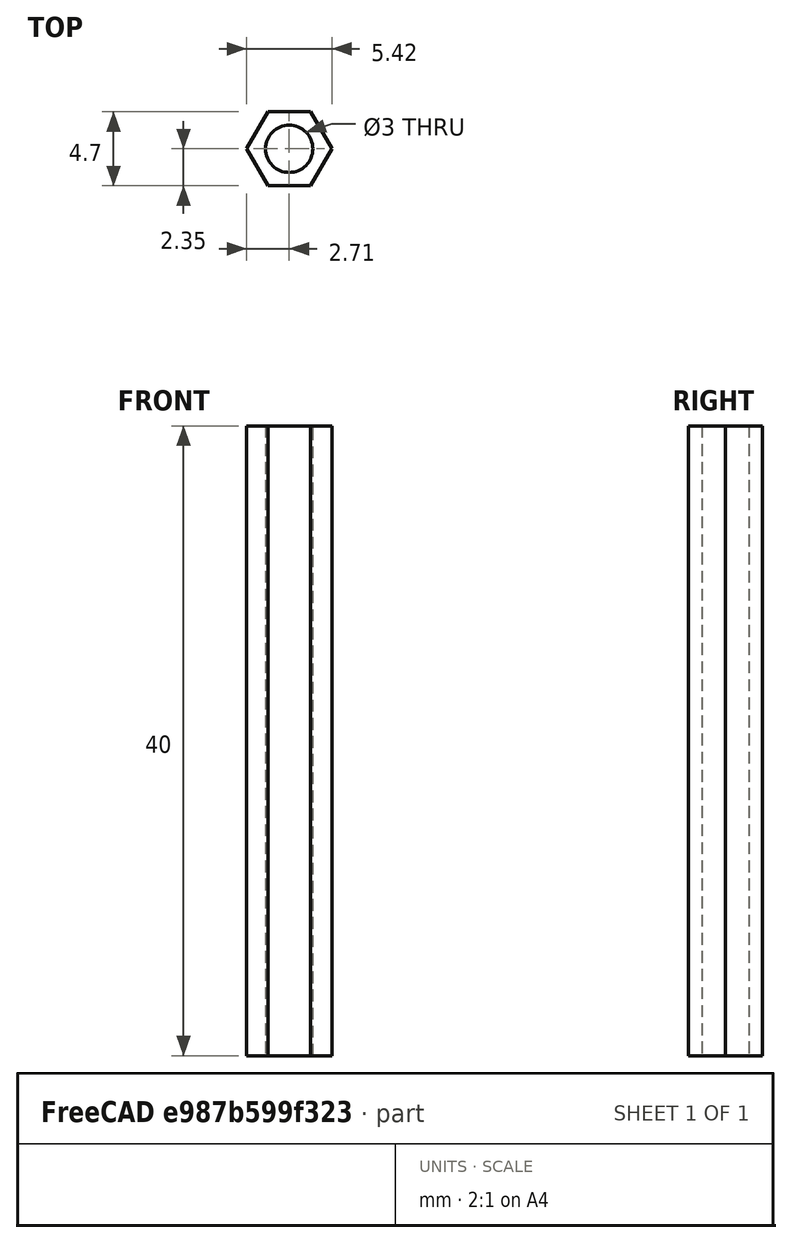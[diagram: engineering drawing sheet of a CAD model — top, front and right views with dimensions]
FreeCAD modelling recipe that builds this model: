
FCSTD DOCUMENT  (FreeCAD 0.18.4R)
Label: coxial_M3_40mm
License: All rights reserved
LicenseURL: http://en.wikipedia.org/wiki/All_rights_reserved
objects: Sketcher::SketchObject×1, PartDesign::Pad×1, PartDesign::Body×1
note: 4 computed .brp shape members not serialized (recipe doc carries the construction recipe); baked Part::Feature solids carry a one-line shape summary decoded from their .brp

FEATURE [Sketcher::SketchObject] Sketch
  MapMode = 5
  Support = -> [XY_Plane001]
  sketch-geometry (8):
    g0: Circle CenterX=0 CenterY=0 CenterZ=0 NormalX=0 NormalY=0 NormalZ=1 AngleXU=0 Radius=1.5
    g1: LineSegment StartX=-1.35677 StartY=-2.35 StartZ=0 EndX=1.35677 EndY=-2.35 EndZ=0
    g2: LineSegment StartX=1.35677 StartY=-2.35 StartZ=0 EndX=2.71355 EndY=-6.306e-13 EndZ=0
    g3: LineSegment StartX=2.71355 StartY=-6.306e-13 StartZ=0 EndX=1.35677 EndY=2.35 EndZ=0
    g4: LineSegment StartX=1.35677 StartY=2.35 StartZ=0 EndX=-1.35677 EndY=2.35 EndZ=0
    g5: LineSegment StartX=-1.35677 StartY=2.35 StartZ=0 EndX=-2.71355 EndY=8.93e-14 EndZ=0
    g6: LineSegment StartX=-2.71355 StartY=8.93e-14 StartZ=0 EndX=-1.35677 EndY=-2.35 EndZ=0
    g7: Circle [constr] CenterX=0 CenterY=0 CenterZ=0 NormalX=0 NormalY=0 NormalZ=1 AngleXU=0 Radius=2.71355
  constraints (18):
    c: Radius(g0) = 1.5
    c: Coincident(g1,g2)
    c: Coincident(g2,g3)
    c: Coincident(g3,g4)
    c: Coincident(g4,g5)
    c: Coincident(g5,g6)
    c: Coincident(g6,g1)
    c: Equal(g1, g2-g6) x5
    c: PointOnObject(g1,g7)
    c: PointOnObject(g2,g7)
    c: PointOnObject(g3,g7)
    c: PointOnObject(g4,g7)
    c: PointOnObject(g5,g7)
    c: PointOnObject(g6,g7)
    c: Distance(g2,g4) = 4.7
    c: Coincident(g7,g0)
    c: Coincident(g0,g-1)
    c: Horizontal(g4)
FEATURE [PartDesign::Pad] Pad
  Length = 40
  Length2 = 100
  Profile = -> Sketch
  Type = 0
FEATURE [PartDesign::Body] Body
  Group = -> [Sketch,Pad]
  Origin = -> Origin001
  Tip = -> Pad
